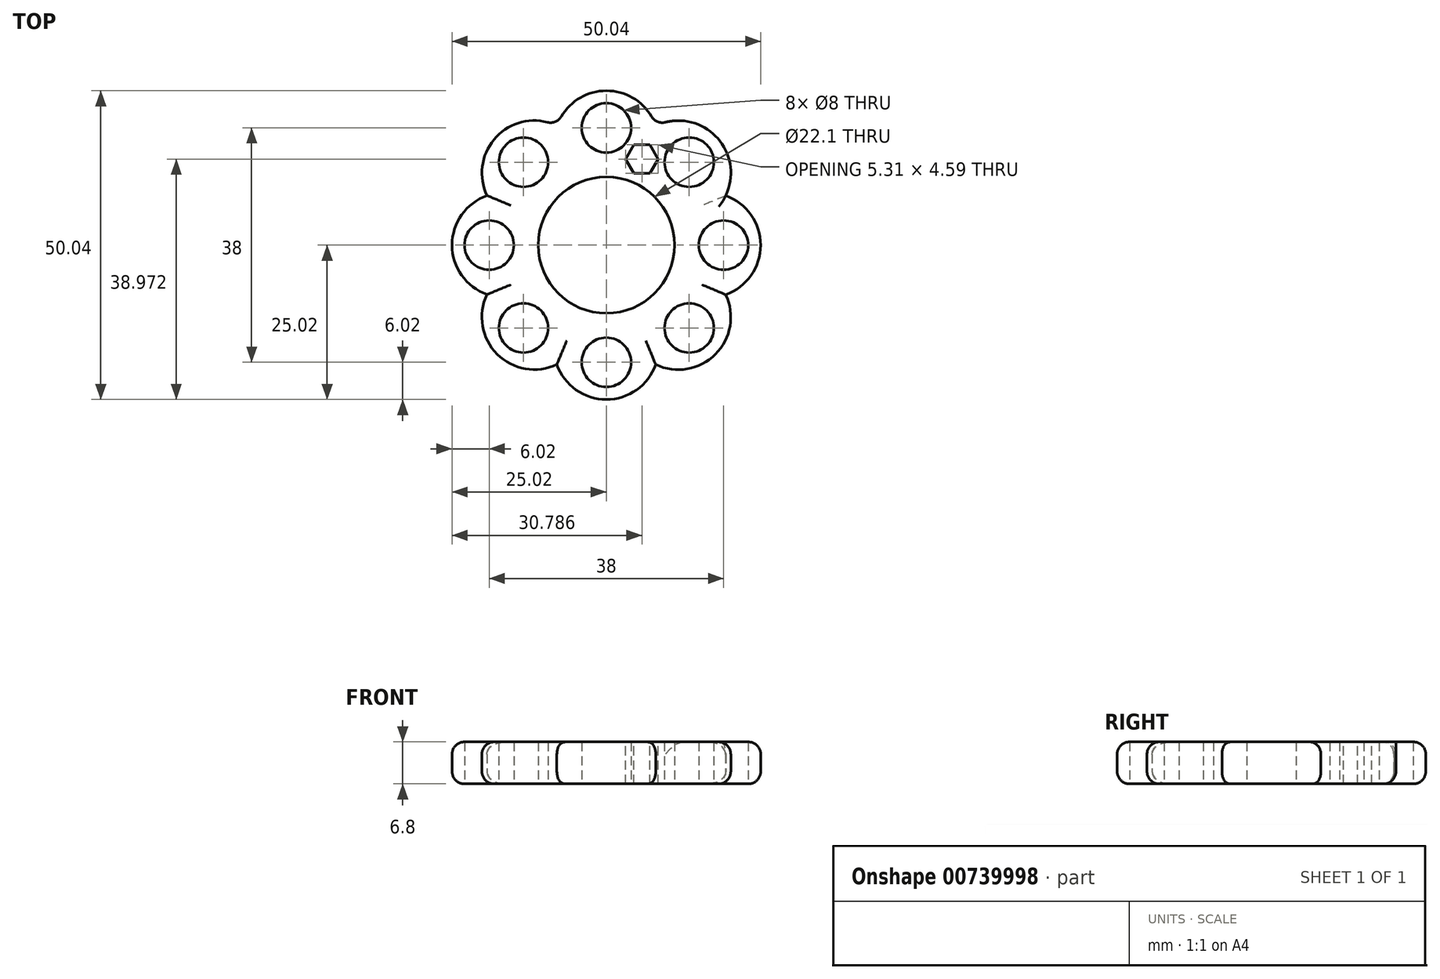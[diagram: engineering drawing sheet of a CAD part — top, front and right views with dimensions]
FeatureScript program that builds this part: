
annotation { "Feature Type Name" : "Feature", "Feature Type Description" : "" }
export const myFeature = defineFeature(function(context is Context, id is Id, definition is map)
    precondition{}
    {
        {
            var Q0;
            Q0=qCreatedBy(makeId("Top.planeOp"),FACE);
            var sketch = newSketch(context, id + "F0", { "sketchPlane" : qUnion([Q0])});
            skCircle(sketch, "E0", {"center": v(0, 0) * mm, "radius": 11.05 * mm});
            skCircle(sketch, "E1.0", {"center": v(0, 0) * mm, "radius": 13.05 * mm});
            skCircle(sketch, "E2", {"center": v(0, 19) * mm, "radius": 4 * mm});
            skCircle(sketch, "E3", {"center": v(0, 16.52) * mm, "radius": 8.5 * mm});
            skPoint(sketch, "E3.first.point", {"position": v(-5.78, 26.53) * mm});
            skPoint(sketch, "E3.second.point", {"position": v(6.58, 27.89) * mm});
            skPoint(sketch, "E3.third.point", {"position": v(0, 11.05) * mm});
            skSolve(sketch);
        }
        {
            var Q0;
            Q0=makeQuery(id+"F0.imprint","IMPRINT",FACE,{"disambiguationData":[TD([[makeQuery(id+"F0.imprint","IMPRINT",EDGE,{"derivedFrom":sQuery(id+"F0.wireOp",EDGE,"E2")}),-1.0]])]});
            var Q1;
            {var subQ0=sQuery(id+"F0.wireOp",EDGE,"E3");var subQ1=sQuery(id+"F0.wireOp",EDGE,"E1.0");var subQ2=makeQuery(id+"F0.imprint","INTERSECT",VERTEX,{"disambiguationData":[OD(0.0)],"derivedFrom":[subQ1,subQ0]});Q1=makeQuery(id+"F0.imprint","IMPRINT",FACE,{"disambiguationData":[TD([[makeQuery(id+"F0.imprint","IMPRINT",EDGE,{"disambiguationData":[TD([[subQ2,-1.0]])],"derivedFrom":subQ1}),1.0]])]});}
            var Q2;
            {var subQ0=sQuery(id+"F0.wireOp",EDGE,"brosbazZ-erjU-CTYZ-AfMW-5ceamOz2Ci2e.top");var subQ1=sQuery(id+"F0.wireOp",EDGE,"E0");var subQ2=makeQuery(id+"F0.imprint","INTERSECT",VERTEX,{"derivedFrom":[subQ1,subQ0]});Q2=makeQuery(id+"F0.imprint","IMPRINT",FACE,{"disambiguationData":[TD([[makeQuery(id+"F0.imprint","IMPRINT",EDGE,{"disambiguationData":[TD([[subQ2,-1.0]])],"derivedFrom":subQ1}),-1.0]])]});}
            var Q3;
            {var subQ0=sQuery(id+"F0.wireOp",EDGE,"brosbazZ-erjU-CTYZ-AfMW-5ceamOz2Ci2e.top");var subQ1=sQuery(id+"F0.wireOp",EDGE,"E0");var subQ2=makeQuery(id+"F0.imprint","INTERSECT",VERTEX,{"derivedFrom":[subQ1,subQ0]});Q3=makeQuery(id+"F0.imprint","IMPRINT",FACE,{"disambiguationData":[TD([[makeQuery(id+"F0.imprint","IMPRINT",EDGE,{"disambiguationData":[TD([[subQ2,1.0]])],"derivedFrom":subQ1}),-1.0]])]});}
            extrude(context, id + "F1", {"entities" : qUnion([Q0, Q1, Q2, Q3]), "depth" : 6.8 * mm, "offsetDistance" : 25 * mm});
        }
        {
            var Q0;
            Q0=makeQuery(id+"F1.opExtrude","SWEPT_BODY",BODY,{"disambiguationData":[OSD([sQuery(id+"F0.wireOp",EDGE,"E0"),sQuery(id+"F0.wireOp",EDGE,"E1.0"),sQuery(id+"F0.wireOp",EDGE,"E2"),sQuery(id+"F0.wireOp",EDGE,"E3")])]});
            var Q1;
            Q1=makeQuery(id+"F1.opExtrude","CAP_EDGE",EDGE,{"disambiguationData":[OSD([sQuery(id+"F0.wireOp",EDGE,"E0")])],"isStart":false});
            circularPattern(context, id + "F2", {"entities" : qUnion([Q0]), "axis" : qUnion([Q1]), "angle" : 360 * degree, "instanceCount" : 8, "equalSpace" : true});
        }
        {
            var Q0;
            Q0=makeQuery(id+"F1.opExtrude","SWEPT_BODY",BODY,{"disambiguationData":[OSD([sQuery(id+"F0.wireOp",EDGE,"E0"),sQuery(id+"F0.wireOp",EDGE,"E1.0"),sQuery(id+"F0.wireOp",EDGE,"E2"),sQuery(id+"F0.wireOp",EDGE,"E3")])]});
            var Q1;
            Q1=makeQuery(id+"F2.opPattern","COPY",BODY,{"derivedFrom":makeQuery(id+"F1.opExtrude","SWEPT_BODY",BODY,{"disambiguationData":[OSD([sQuery(id+"F0.wireOp",EDGE,"E0"),sQuery(id+"F0.wireOp",EDGE,"E1.0"),sQuery(id+"F0.wireOp",EDGE,"E2"),sQuery(id+"F0.wireOp",EDGE,"E3")])]}),"instanceName":"4"});
            var Q2;
            Q2=makeQuery(id+"F2.opPattern","COPY",BODY,{"derivedFrom":makeQuery(id+"F1.opExtrude","SWEPT_BODY",BODY,{"disambiguationData":[OSD([sQuery(id+"F0.wireOp",EDGE,"E0"),sQuery(id+"F0.wireOp",EDGE,"E1.0"),sQuery(id+"F0.wireOp",EDGE,"E2"),sQuery(id+"F0.wireOp",EDGE,"E3")])]}),"instanceName":"3"});
            var Q3;
            Q3=makeQuery(id+"F2.opPattern","COPY",BODY,{"derivedFrom":makeQuery(id+"F1.opExtrude","SWEPT_BODY",BODY,{"disambiguationData":[OSD([sQuery(id+"F0.wireOp",EDGE,"E0"),sQuery(id+"F0.wireOp",EDGE,"E1.0"),sQuery(id+"F0.wireOp",EDGE,"E2"),sQuery(id+"F0.wireOp",EDGE,"E3")])]}),"instanceName":"2"});
            var Q4;
            Q4=makeQuery(id+"F2.opPattern","COPY",BODY,{"derivedFrom":makeQuery(id+"F1.opExtrude","SWEPT_BODY",BODY,{"disambiguationData":[OSD([sQuery(id+"F0.wireOp",EDGE,"E0"),sQuery(id+"F0.wireOp",EDGE,"E1.0"),sQuery(id+"F0.wireOp",EDGE,"E2"),sQuery(id+"F0.wireOp",EDGE,"E3")])]}),"instanceName":"1"});
            var Q5;
            Q5=makeQuery(id+"F2.opPattern","COPY",BODY,{"derivedFrom":makeQuery(id+"F1.opExtrude","SWEPT_BODY",BODY,{"disambiguationData":[OSD([sQuery(id+"F0.wireOp",EDGE,"E0"),sQuery(id+"F0.wireOp",EDGE,"E1.0"),sQuery(id+"F0.wireOp",EDGE,"E2"),sQuery(id+"F0.wireOp",EDGE,"E3")])]}),"instanceName":"5"});
            var Q6;
            Q6=makeQuery(id+"F2.opPattern","COPY",BODY,{"derivedFrom":makeQuery(id+"F1.opExtrude","SWEPT_BODY",BODY,{"disambiguationData":[OSD([sQuery(id+"F0.wireOp",EDGE,"E0"),sQuery(id+"F0.wireOp",EDGE,"E1.0"),sQuery(id+"F0.wireOp",EDGE,"E2"),sQuery(id+"F0.wireOp",EDGE,"E3")])]}),"instanceName":"7"});
            var Q7;
            Q7=makeQuery(id+"F2.opPattern","COPY",BODY,{"derivedFrom":makeQuery(id+"F1.opExtrude","SWEPT_BODY",BODY,{"disambiguationData":[OSD([sQuery(id+"F0.wireOp",EDGE,"E0"),sQuery(id+"F0.wireOp",EDGE,"E1.0"),sQuery(id+"F0.wireOp",EDGE,"E2"),sQuery(id+"F0.wireOp",EDGE,"E3")])]}),"instanceName":"6"});
            booleanBodies(context, id + "F3", {"operationType" : BooleanOperationType.UNION, "tools" : qUnion([Q0, Q1, Q2, Q3, Q4, Q5, Q6, Q7])});
        }
        {
            var Q0;
            Q0=makeQuery(id+"F2.opPattern","COPY",EDGE,{"derivedFrom":makeQuery(id+"F1.opExtrude","CAP_EDGE",EDGE,{"disambiguationData":[OSD([sQuery(id+"F0.wireOp",EDGE,"E3")])],"isStart":true}),"instanceName":"5"});
            var Q1;
            Q1=makeQuery(id+"F2.opPattern","COPY",EDGE,{"derivedFrom":makeQuery(id+"F1.opExtrude","CAP_EDGE",EDGE,{"disambiguationData":[OSD([sQuery(id+"F0.wireOp",EDGE,"E3")])],"isStart":true}),"instanceName":"4"});
            var Q2;
            Q2=makeQuery(id+"F2.opPattern","COPY",EDGE,{"derivedFrom":makeQuery(id+"F1.opExtrude","CAP_EDGE",EDGE,{"disambiguationData":[OSD([sQuery(id+"F0.wireOp",EDGE,"E3")])],"isStart":true}),"instanceName":"3"});
            var Q3;
            Q3=makeQuery(id+"F2.opPattern","COPY",EDGE,{"derivedFrom":makeQuery(id+"F1.opExtrude","CAP_EDGE",EDGE,{"disambiguationData":[OSD([sQuery(id+"F0.wireOp",EDGE,"E3")])],"isStart":true}),"instanceName":"2"});
            var Q4;
            Q4=makeQuery(id+"F2.opPattern","COPY",EDGE,{"derivedFrom":makeQuery(id+"F1.opExtrude","CAP_EDGE",EDGE,{"disambiguationData":[OSD([sQuery(id+"F0.wireOp",EDGE,"E3")])],"isStart":true}),"instanceName":"1"});
            var Q5;
            Q5=makeQuery(id+"F1.opExtrude","CAP_EDGE",EDGE,{"disambiguationData":[OSD([sQuery(id+"F0.wireOp",EDGE,"E3")])],"isStart":true});
            var Q6;
            Q6=makeQuery(id+"F2.opPattern","COPY",EDGE,{"derivedFrom":makeQuery(id+"F1.opExtrude","CAP_EDGE",EDGE,{"disambiguationData":[OSD([sQuery(id+"F0.wireOp",EDGE,"E3")])],"isStart":true}),"instanceName":"7"});
            var Q7;
            Q7=makeQuery(id+"F2.opPattern","COPY",EDGE,{"derivedFrom":makeQuery(id+"F1.opExtrude","CAP_EDGE",EDGE,{"disambiguationData":[OSD([sQuery(id+"F0.wireOp",EDGE,"E3")])],"isStart":true}),"instanceName":"6"});
            var Q8;
            Q8=makeQuery(id+"F1.opExtrude","SWEPT_FACE",FACE,{"disambiguationData":[OSD([sQuery(id+"F0.wireOp",EDGE,"E3")])]});
            var Q9;
            Q9=makeQuery(id+"F2.opPattern","COPY",EDGE,{"derivedFrom":makeQuery(id+"F1.opExtrude","CAP_EDGE",EDGE,{"disambiguationData":[OSD([sQuery(id+"F0.wireOp",EDGE,"E3")])],"isStart":false}),"instanceName":"1"});
            var Q10;
            Q10=makeQuery(id+"F2.opPattern","COPY",EDGE,{"derivedFrom":makeQuery(id+"F1.opExtrude","CAP_EDGE",EDGE,{"disambiguationData":[OSD([sQuery(id+"F0.wireOp",EDGE,"E3")])],"isStart":false}),"instanceName":"2"});
            var Q11;
            Q11=makeQuery(id+"F2.opPattern","COPY",EDGE,{"derivedFrom":makeQuery(id+"F1.opExtrude","CAP_EDGE",EDGE,{"disambiguationData":[OSD([sQuery(id+"F0.wireOp",EDGE,"E3")])],"isStart":false}),"instanceName":"6"});
            var Q12;
            Q12=makeQuery(id+"F2.opPattern","COPY",EDGE,{"derivedFrom":makeQuery(id+"F1.opExtrude","CAP_EDGE",EDGE,{"disambiguationData":[OSD([sQuery(id+"F0.wireOp",EDGE,"E3")])],"isStart":false}),"instanceName":"5"});
            var Q13;
            Q13=makeQuery(id+"F2.opPattern","COPY",EDGE,{"derivedFrom":makeQuery(id+"F1.opExtrude","CAP_EDGE",EDGE,{"disambiguationData":[OSD([sQuery(id+"F0.wireOp",EDGE,"E3")])],"isStart":false}),"instanceName":"4"});
            var Q14;
            Q14=makeQuery(id+"F2.opPattern","COPY",EDGE,{"derivedFrom":makeQuery(id+"F1.opExtrude","CAP_EDGE",EDGE,{"disambiguationData":[OSD([sQuery(id+"F0.wireOp",EDGE,"E3")])],"isStart":false}),"instanceName":"3"});
            fillet(context, id + "F4", {"entities" : qUnion([Q0, Q1, Q2, Q3, Q4, Q5, Q6, Q7, Q8, Q9, Q10, Q11, Q12, Q13, Q14]), "radius" : 2 * mm, "tangentPropagation" : true, "allowEdgeOverflow" : false});
        }
        {
            var Q0;
            {var subQ0=makeQuery(id+"F1.opExtrude","CAP_FACE",FACE,{"disambiguationData":[OSD([sQuery(id+"F0.wireOp",EDGE,"E0"),sQuery(id+"F0.wireOp",EDGE,"E1.0"),sQuery(id+"F0.wireOp",EDGE,"E2"),sQuery(id+"F0.wireOp",EDGE,"E3")])],"isStart":false});Q0=makeQuery(id+"F3.opBoolean","MERGE",FACE,{"derivedFrom":[subQ0,makeQuery(id+"F2.opPattern","COPY",FACE,{"derivedFrom":subQ0,"instanceName":"1"}),makeQuery(id+"F2.opPattern","COPY",FACE,{"derivedFrom":subQ0,"instanceName":"2"}),makeQuery(id+"F2.opPattern","COPY",FACE,{"derivedFrom":subQ0,"instanceName":"3"}),makeQuery(id+"F2.opPattern","COPY",FACE,{"derivedFrom":subQ0,"instanceName":"4"}),makeQuery(id+"F2.opPattern","COPY",FACE,{"derivedFrom":subQ0,"instanceName":"5"}),makeQuery(id+"F2.opPattern","COPY",FACE,{"derivedFrom":subQ0,"instanceName":"6"}),makeQuery(id+"F2.opPattern","COPY",FACE,{"derivedFrom":subQ0,"instanceName":"7"})]});}
            var sketch = newSketch(context, id + "F5", { "sketchPlane" : qUnion([Q0])});
            skCircle(sketch, "E4.cCircle", {"center": v(5.77, 13.95) * mm, "radius": 2.3 * mm, "construction": true});
            skLineSegment(sketch, "E4.0", {"start": v(7.1, 11.65) * mm, "end": v(4.44, 11.65) * mm});
            skLineSegment(sketch, "E4.1", {"start": v(4.44, 11.65) * mm, "end": v(3.11, 13.95) * mm});
            skLineSegment(sketch, "E4.2", {"start": v(3.11, 13.95) * mm, "end": v(4.44, 16.25) * mm});
            skLineSegment(sketch, "E4.3", {"start": v(4.44, 16.25) * mm, "end": v(7.1, 16.25) * mm});
            skLineSegment(sketch, "E4.4", {"start": v(7.1, 16.25) * mm, "end": v(8.42, 13.95) * mm});
            skLineSegment(sketch, "E4.5", {"start": v(8.42, 13.95) * mm, "end": v(7.1, 11.65) * mm});
            skPoint(sketch, "E4.0.midPoint", {"position": v(5.77, 11.65) * mm});
            skSolve(sketch);
        }
        {
            var Q0;
            Q0=makeQuery(id+"F5.imprint","IMPRINT",FACE,{"disambiguationData":[TD([[makeQuery(id+"F5.imprint","IMPRINT",EDGE,{"derivedFrom":sQuery(id+"F5.wireOp",EDGE,"E4.0")}),-1.0]])]});
            extrude(context, id + "F6", {"entities" : qUnion([Q0]), "operationType" : NewBodyOperationType.REMOVE, "oppositeDirection" : true, "depth" : 9 * mm, "offsetDistance" : 25 * mm});
        }
    });
